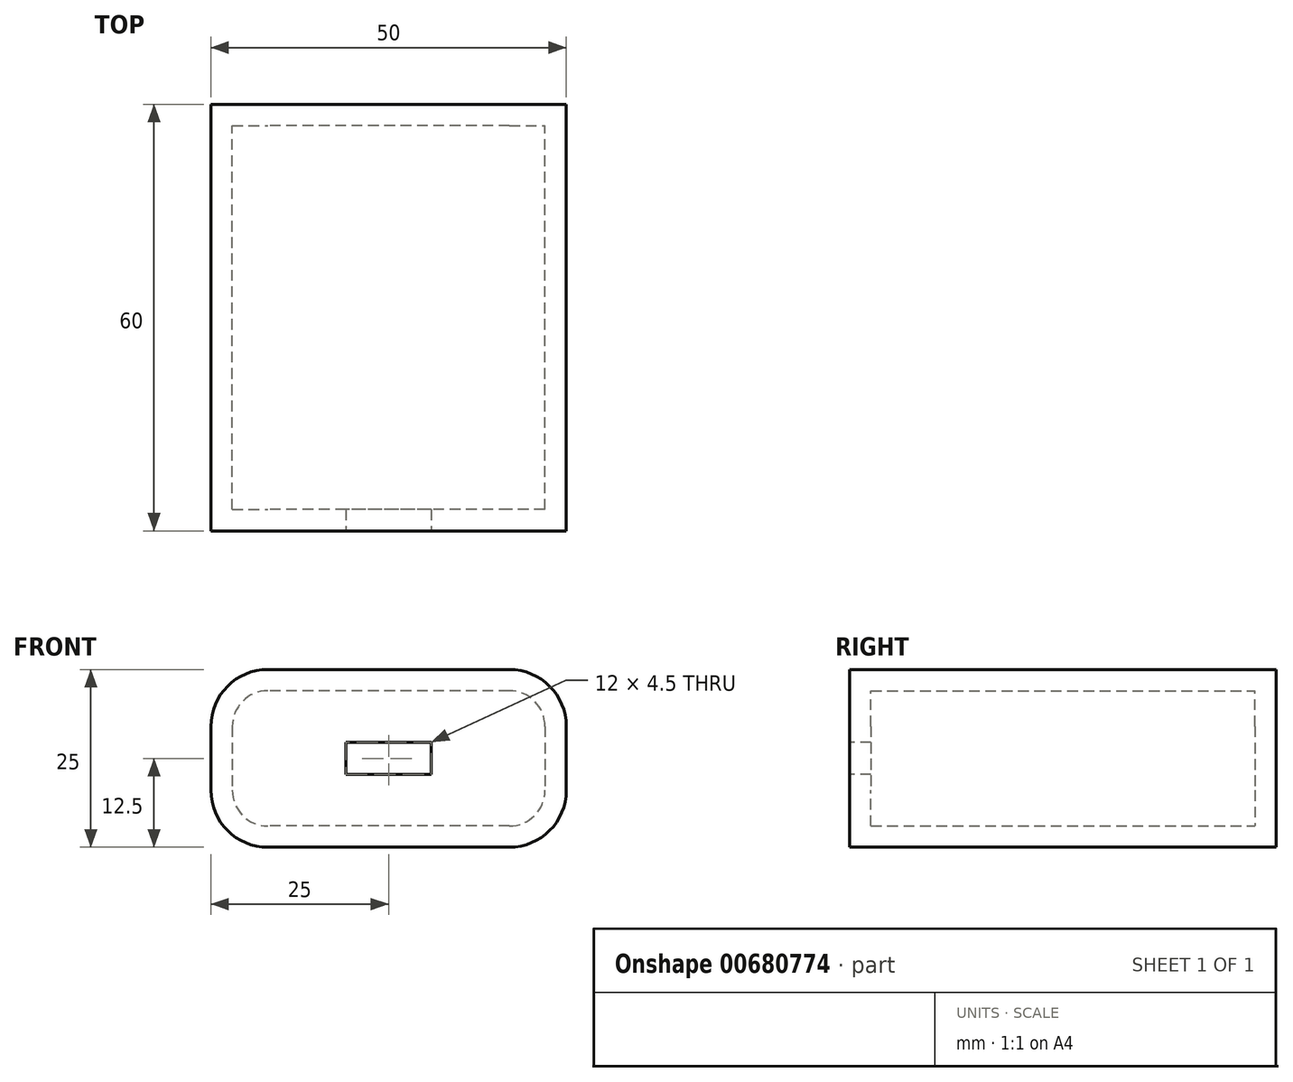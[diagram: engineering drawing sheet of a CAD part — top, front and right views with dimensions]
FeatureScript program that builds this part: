
annotation { "Feature Type Name" : "Feature", "Feature Type Description" : "" }
export const myFeature = defineFeature(function(context is Context, id is Id, definition is map)
    precondition{}
    {
        {
            var Q0;
            Q0=qCreatedBy(makeId("Top.planeOp"),FACE);
            var sketch = newSketch(context, id + "F0", { "sketchPlane" : qUnion([Q0])});
            skLineSegment(sketch, "E0.bottom", {"start": v(25, 30) * mm, "end": v(-25, 30) * mm});
            skLineSegment(sketch, "E0.top", {"start": v(25, -30) * mm, "end": v(-25, -30) * mm});
            skLineSegment(sketch, "E0.left", {"start": v(25, 30) * mm, "end": v(25, -30) * mm});
            skLineSegment(sketch, "E0.right", {"start": v(-25, 30) * mm, "end": v(-25, -30) * mm});
            skPoint(sketch, "E0.middle", {"position": v(0, 0) * mm});
            skSolve(sketch);
        }
        {
            var Q0;
            Q0 = qSketchRegion(id + "F0", true);
            extrude(context, id + "F1", {"entities" : qUnion([Q0]), "depth" : 25 * mm, "offsetDistance" : 25 * mm});
        }
        {
            var Q0;
            Q0=makeQuery(id+"F1.opExtrude","CAP_EDGE",EDGE,{"disambiguationData":[OSD([sQuery(id+"F0.wireOp",EDGE,"E0.left")])],"isStart":false});
            var Q1;
            Q1=makeQuery(id+"F1.opExtrude","CAP_EDGE",EDGE,{"disambiguationData":[OSD([sQuery(id+"F0.wireOp",EDGE,"E0.left")])],"isStart":true});
            var Q2;
            Q2=makeQuery(id+"F1.opExtrude","CAP_EDGE",EDGE,{"disambiguationData":[OSD([sQuery(id+"F0.wireOp",EDGE,"E0.right")])],"isStart":true});
            var Q3;
            Q3=makeQuery(id+"F1.opExtrude","CAP_EDGE",EDGE,{"disambiguationData":[OSD([sQuery(id+"F0.wireOp",EDGE,"E0.right")])],"isStart":false});
            fillet(context, id + "F2", {"entities" : qUnion([Q0, Q1, Q2, Q3]), "radius" : 8 * mm, "tangentPropagation" : true, "allowEdgeOverflow" : false});
        }
        {
            var Q0;
            Q0=makeQuery(id+"F1.opExtrude","SWEPT_FACE",FACE,{"disambiguationData":[OSD([sQuery(id+"F0.wireOp",EDGE,"E0.bottom")])]});
            var Q1;
            {var subQ0=sQuery(id+"F0.wireOp",EDGE,"E0.right");Q1=makeQuery(id+"F2.opFillet","BLEND_FACE",FACE,{"disambiguationData":[OSD([subQ0]),TDD([makeQuery(id+"F1.opExtrude","CAP_EDGE",EDGE,{"disambiguationData":[OSD([subQ0])],"isStart":true})])]});}
            var Q2;
            Q2=makeQuery(id+"F1.opExtrude","SWEPT_FACE",FACE,{"disambiguationData":[OSD([sQuery(id+"F0.wireOp",EDGE,"E0.left")])]});
            var Q3;
            {var subQ0=sQuery(id+"F0.wireOp",EDGE,"E0.right");Q3=makeQuery(id+"F2.opFillet","BLEND_FACE",FACE,{"disambiguationData":[OSD([subQ0]),TDD([makeQuery(id+"F1.opExtrude","CAP_EDGE",EDGE,{"disambiguationData":[OSD([subQ0])],"isStart":false})])]});}
            var Q4;
            Q4=makeQuery(id+"F1.opExtrude","CAP_FACE",FACE,{"disambiguationData":[OSD([sQuery(id+"F0.wireOp",EDGE,"E0.bottom"),sQuery(id+"F0.wireOp",EDGE,"E0.top"),sQuery(id+"F0.wireOp",EDGE,"E0.left"),sQuery(id+"F0.wireOp",EDGE,"E0.right")])],"isStart":true});
            var Q5;
            {var subQ0=sQuery(id+"F0.wireOp",EDGE,"E0.left");Q5=makeQuery(id+"F2.opFillet","BLEND_FACE",FACE,{"disambiguationData":[OSD([subQ0]),TDD([makeQuery(id+"F1.opExtrude","CAP_EDGE",EDGE,{"disambiguationData":[OSD([subQ0])],"isStart":false})])]});}
            var Q6;
            Q6=makeQuery(id+"F1.opExtrude","CAP_FACE",FACE,{"disambiguationData":[OSD([sQuery(id+"F0.wireOp",EDGE,"E0.bottom"),sQuery(id+"F0.wireOp",EDGE,"E0.top"),sQuery(id+"F0.wireOp",EDGE,"E0.left"),sQuery(id+"F0.wireOp",EDGE,"E0.right")])],"isStart":false});
            var Q7;
            Q7=makeQuery(id+"F1.opExtrude","SWEPT_FACE",FACE,{"disambiguationData":[OSD([sQuery(id+"F0.wireOp",EDGE,"E0.right")])]});
            var Q8;
            {var subQ0=sQuery(id+"F0.wireOp",EDGE,"E0.left");Q8=makeQuery(id+"F2.opFillet","BLEND_FACE",FACE,{"disambiguationData":[OSD([subQ0]),TDD([makeQuery(id+"F1.opExtrude","CAP_EDGE",EDGE,{"disambiguationData":[OSD([subQ0])],"isStart":true})])]});}
            var Q9;
            Q9=makeQuery(id+"F1.opExtrude","SWEPT_FACE",FACE,{"disambiguationData":[OSD([sQuery(id+"F0.wireOp",EDGE,"E0.top")])]});
            var Q10;
            Q10=makeQuery(id+"F1.opExtrude","SWEPT_BODY",BODY,{"disambiguationData":[OSD([sQuery(id+"F0.wireOp",EDGE,"E0.bottom"),sQuery(id+"F0.wireOp",EDGE,"E0.top"),sQuery(id+"F0.wireOp",EDGE,"E0.left"),sQuery(id+"F0.wireOp",EDGE,"E0.right")])]});
            shell(context, id + "F3", {"isHollow" : true, "entities" : qUnion([Q0, Q1, Q2, Q3, Q4, Q5, Q6, Q7, Q8, Q9]), "parts" : qUnion([Q10]), "thickness" : 3 * mm});
        }
        {
            var Q0;
            Q0=makeQuery(id+"F1.opExtrude","SWEPT_FACE",FACE,{"disambiguationData":[OSD([sQuery(id+"F0.wireOp",EDGE,"E0.top")])]});
            var sketch = newSketch(context, id + "F4", { "sketchPlane" : qUnion([Q0])});
            skLineSegment(sketch, "E1", {"start": v(-25, 12.5) * mm, "end": v(25, 12.5) * mm, "construction": true});
            skLineSegment(sketch, "E2", {"start": v(0, 0) * mm, "end": v(0, 25) * mm, "construction": true});
            skLineSegment(sketch, "E3.bottom", {"start": v(6, 14.75) * mm, "end": v(-6, 14.75) * mm});
            skLineSegment(sketch, "E3.top", {"start": v(6, 10.25) * mm, "end": v(-6, 10.25) * mm});
            skLineSegment(sketch, "E3.left", {"start": v(6, 14.75) * mm, "end": v(6, 10.25) * mm});
            skLineSegment(sketch, "E3.right", {"start": v(-6, 14.75) * mm, "end": v(-6, 10.25) * mm});
            skPoint(sketch, "E3.middle", {"position": v(0, 12.5) * mm});
            skSolve(sketch);
        }
        {
            var Q0;
            Q0 = qSketchRegion(id + "F4", true);
            extrude(context, id + "F5", {"entities" : qUnion([Q0]), "operationType" : NewBodyOperationType.REMOVE, "oppositeDirection" : true, "depth" : 3 * mm, "offsetDistance" : 25 * mm});
        }
    });
